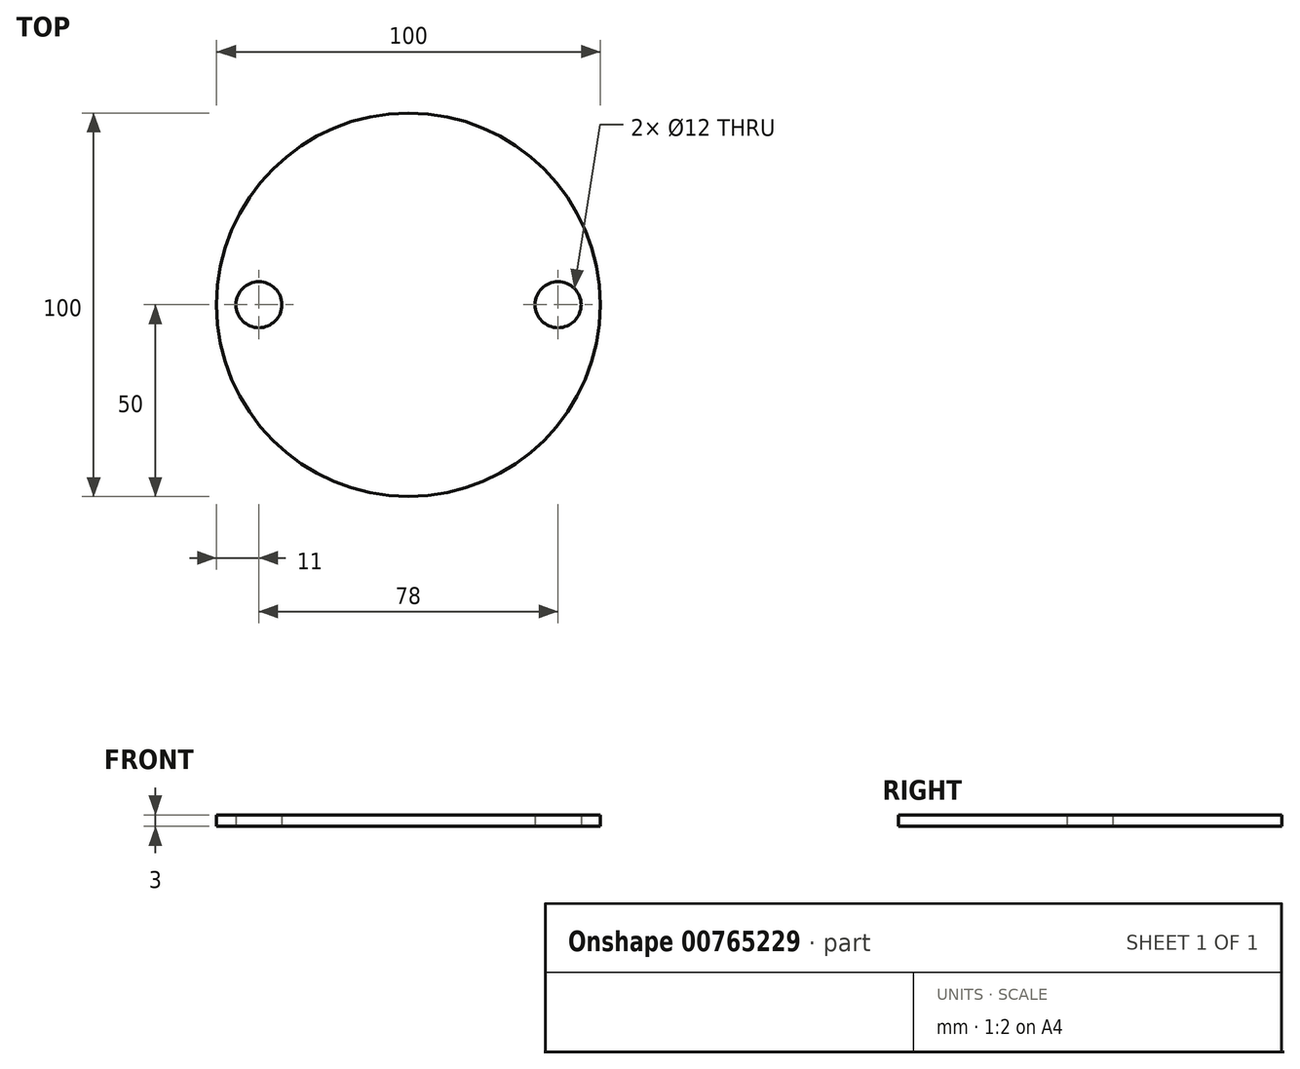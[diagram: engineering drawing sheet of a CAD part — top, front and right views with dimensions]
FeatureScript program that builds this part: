
annotation { "Feature Type Name" : "Feature", "Feature Type Description" : "" }
export const myFeature = defineFeature(function(context is Context, id is Id, definition is map)
    precondition{}
    {
        {
            var Q0;
            Q0=qCreatedBy(makeId("Top.planeOp"),FACE);
            var sketch = newSketch(context, id + "F0", { "sketchPlane" : qUnion([Q0])});
            skCircle(sketch, "E0", {"center": v(0, 0) * mm, "radius": 50 * mm});
            skCircle(sketch, "E1", {"center": v(-39, 0) * mm, "radius": 6 * mm});
            skCircle(sketch, "E2", {"center": v(39, 0) * mm, "radius": 6 * mm});
            skSolve(sketch);
        }
        {
            var Q0;
            Q0=makeQuery(id+"F0.imprint","IMPRINT",FACE,{"disambiguationData":[TD([[makeQuery(id+"F0.imprint","IMPRINT",EDGE,{"derivedFrom":sQuery(id+"F0.wireOp",EDGE,"E0")}),1.0]])]});
            extrude(context, id + "F1", {"entities" : qUnion([Q0]), "depth" : 3 * mm, "offsetDistance" : 25 * mm});
        }
    });
